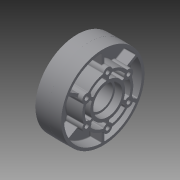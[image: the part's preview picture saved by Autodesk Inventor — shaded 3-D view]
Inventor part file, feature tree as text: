
AUTODESK INVENTOR PART (.ipt)
format: ipt  version: 2014 SP1 (Build 180222100, 222)  size: 2,020,864 bytes
history: native  units: in
note: dims shown in document units (in); Inventor stores cm internally (conversion verified against a paired STEP export)
features: fillet x2, imported_body x2, other x1
ambient origin geometry x8: Origin, YZ Plane, XZ Plane, XY Plane, X Axis, Y Axis, Z Axis, Center Point
bodies: Body1 (feature_tree), Body2 (feature_tree)
feature tree (5):
  fillet  "Fillet10"  [1 undecoded]
  other  "4in 2013 Hub.ipt1"
  fillet  "Fillet9"  [1 undecoded]
  imported_body  "Base1"
  imported_body  "Base2"
note: 2 required parameter values undecoded (feature->parameter linkage not recoverable at this tier; creation-order binding heuristic only, values carry confidence <= 0.55)
